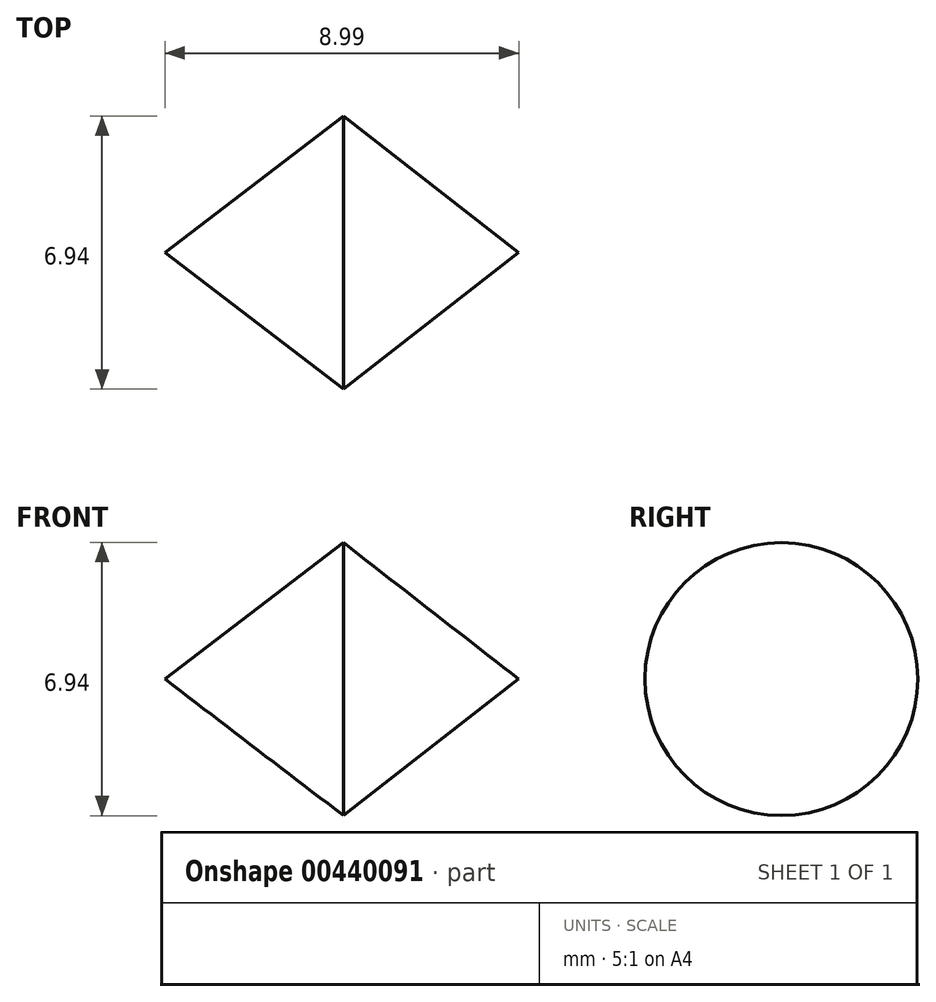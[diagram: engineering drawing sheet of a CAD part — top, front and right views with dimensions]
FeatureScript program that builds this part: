
annotation { "Feature Type Name" : "Feature", "Feature Type Description" : "" }
export const myFeature = defineFeature(function(context is Context, id is Id, definition is map)
    precondition{}
    {
        {
            var Q0;
            Q0=qCreatedBy(makeId("Front.planeOp"),FACE);
            var sketch = newSketch(context, id + "F0", { "sketchPlane" : qUnion([Q0])});
            skLineSegment(sketch, "E0", {"start": v(0, 0) * mm, "end": v(4.46, 0) * mm, "construction": true});
            skLineSegment(sketch, "E1", {"start": v(0, 0) * mm, "end": v(-4.53, 0) * mm, "construction": true});
            skLineSegment(sketch, "E2", {"start": v(-4.53, 0) * mm, "end": v(0, 3.47) * mm});
            skLineSegment(sketch, "E3", {"start": v(0, 3.47) * mm, "end": v(4.46, 0) * mm});
            skSolve(sketch);
        }
        {
            var Q0;
            Q0=sQuery(id+"F0.wireOp",EDGE,"E2");
            var Q1;
            Q1=sQuery(id+"F0.wireOp",EDGE,"E3");
            var Q2;
            Q2=sQuery(id+"F0.wireOp",EDGE,"E0");
            revolve(context, id + "F1", {"bodyType" : ToolBodyType.SURFACE, "surfaceEntities" : qUnion([Q0, Q1]), "axis" : qUnion([Q2]), "revolveType" : RevolveType.FULL});
        }
    });
